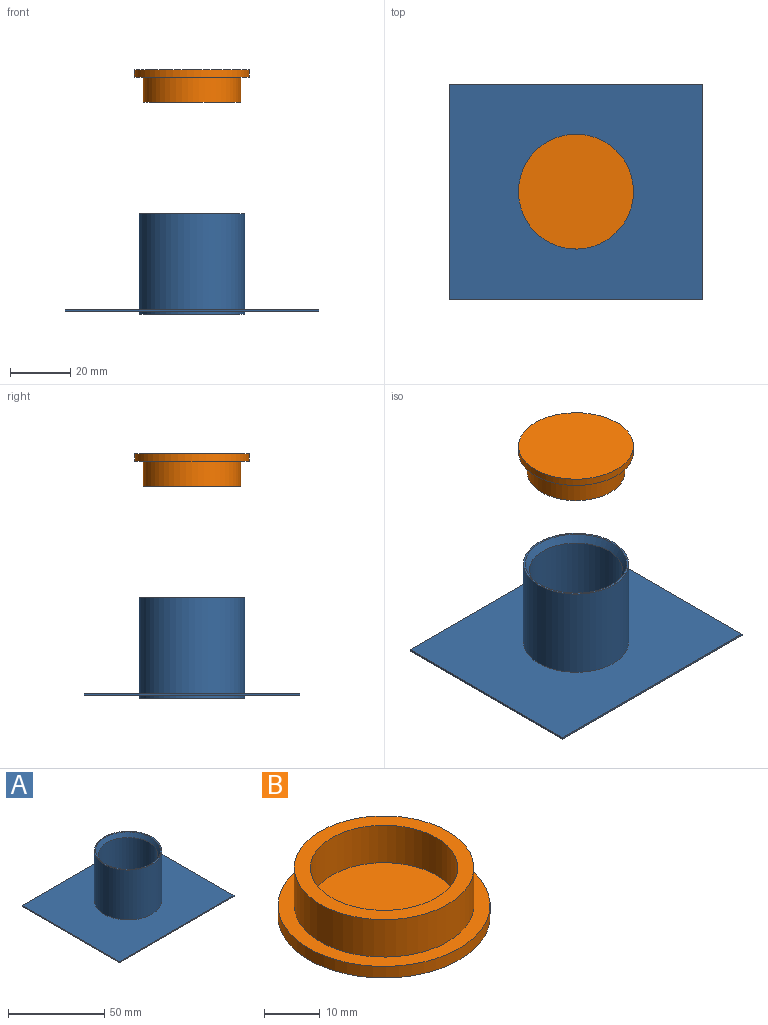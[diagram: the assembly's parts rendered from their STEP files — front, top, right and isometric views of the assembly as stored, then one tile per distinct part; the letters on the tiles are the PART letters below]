
ASSEMBLY  parts=2 mates=1
PART A: 12 faces, bbox 84.1x71.5x33.3 mm
  f0: plane 71.45x0.61mm, normal (1,0,0), area 43.6mm2, adj f1,f3,f4,f5
  f1: plane 84.1x0.61mm, normal (0,1,0), area 51.3mm2, adj f0,f2,f4,f5
  f2: plane 71.45x0.61mm, normal (-1,0,0), area 43.6mm2, adj f1,f3,f4,f5
  f3: plane 84.1x0.61mm, normal (0,-1,0), area 51.3mm2, adj f0,f2,f4,f5
  f4: plane 84.1x71.45mm, normal (0,0,-1), area 5053.7mm2, adj f0,f1,f2,f3,f7
  f5: plane 84.1x71.45mm, normal (0,0,1), area 5053.7mm2, adj f0,f1,f2,f3,f6
  f6: cylinder r=17.44mm len=34.87mm, axis (0,0,-1), area 3473mm2, adj f5,f9
  f7: cylinder r=17.44mm len=34.87mm, axis (0,0,-1), area 112.7mm2, adj f4,f11
  f8: cylinder r=15.43mm len=30.86mm, axis (0,0,-1), area 2985.9mm2, adj f10,f11
  f9: plane 34.87x34.87mm, normal (0,0,1), area 64.5mm2, adj f6,f10
  f10: cone r=15.43mm half-angle=29deg, axis (0,0,1), area 294.4mm2, adj f8,f9
  f11: plane 34.87x34.87mm, normal (0,0,-1), area 207.2mm2, adj f7,f8
PART B: 7 faces, bbox 38.1x38.1x10.8 mm
  f0: cylinder r=19.05mm len=38.1mm, axis (0,0,1), area 304mm2, adj f1,f2
  f1: plane 38.1x38.1mm, normal (0,0,-1), area 1140.1mm2, adj f0
  f2: plane 38.1x38.1mm, normal (0,0,1), area 322.8mm2, adj f0,f4
  f3: cylinder r=13.23mm len=26.47mm, axis (0,0,-1), area 684.3mm2, adj f5,f6
  f4: cylinder r=16.13mm len=32.26mm, axis (0,0,-1), area 834mm2, adj f2,f5
  f5: plane 32.26x32.26mm, normal (0,0,1), area 267.1mm2, adj f3,f4
  f6: plane 26.47x26.47mm, normal (0,0,1), area 550.2mm2, adj f3
PLACE A t=(-16.37,1.56,1.48)mm fixed
PLACE B rot(axis=(0,1,0),180deg) t=(-16.37,1.56,78.42)mm
MATE slider A.f6 <-> B.f0  axis (0,0,-1) through (-16.37,1.56,30.64)mm
